# Revit family: SEQ_A3-CP-Escalator- 6870mm
name_source: partatom
category: Specialty Equipment
revit_build: Autodesk Revit 2016 (Build: 20150220_1215(x64)
units: mm (PartAtom-declared; Revit-internal decimal feet)

## family parameters
Always vertical = Yes
Cut with Voids When Loaded = No
Part Type = Normal
Room Calculation Point = No
Round Connector Dimension = Use Diameter
Shared = No
Work Plane-Based = No

## types (1)
- Escalator 4060 mm Height
    Assembly Code = D1020110
    Body Material = <By Category>
    Description = Escalator
    Landing Length = 2000 mm  [stored 6.56168 ft]
    Length = 11032 mm
    Manufacturer = Revit
    NSteps = 23
    Rise = 4060 mm  [stored 13.3202 ft]
    Stair Width = 800 mm  [stored 2.62467 ft]
    Step Length = 6586 mm
    Step Material = <By Category>
    Total Rise = 5117 mm

note: [stored X ft] marks values corroborated as IEEE doubles in the binary element streams (Revit-internal decimal feet)

## geometry (parser evidence)
native form markers: Sweep x5
no freeform markers — native parametric forms only
